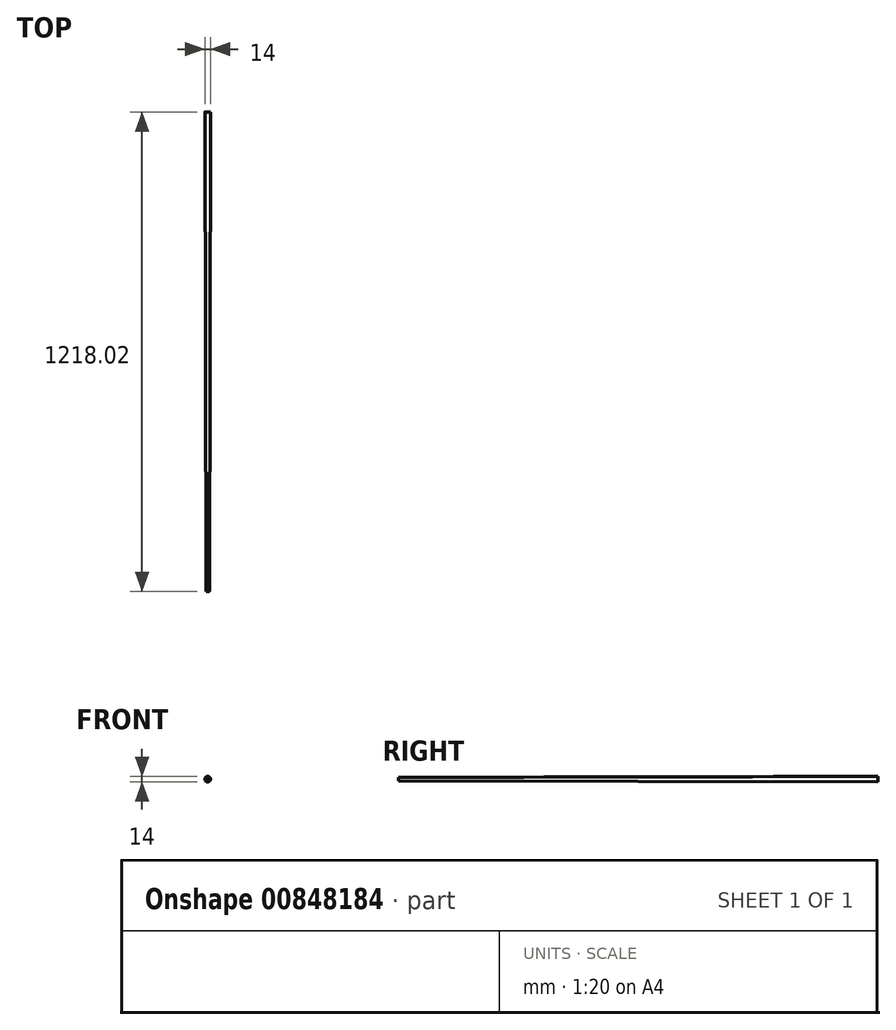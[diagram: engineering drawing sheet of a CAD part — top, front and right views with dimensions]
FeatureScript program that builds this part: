
annotation { "Feature Type Name" : "Feature", "Feature Type Description" : "" }
export const myFeature = defineFeature(function(context is Context, id is Id, definition is map)
    precondition{}
    {
        {
            var Q0;
            Q0=qCreatedBy(makeId("Right.planeOp"),FACE);
            var sketch = newSketch(context, id + "F0", { "sketchPlane" : qUnion([Q0])});
            skLineSegment(sketch, "E0", {"start": v(0, 0) * mm, "end": v(-1218.02, 0) * mm});
            skLineSegment(sketch, "E1", {"start": v(-1218.02, 0) * mm, "end": v(-1218.02, -4.42) * mm});
            skLineSegment(sketch, "E2", {"start": v(0, 0) * mm, "end": v(0, -7) * mm});
            skLineSegment(sketch, "E3", {"start": v(0, -7) * mm, "end": v(-1218.02, -4.42) * mm});
            skSolve(sketch);
        }
        {
            var Q0;
            Q0=makeQuery(id+"F0.imprint","IMPRINT",FACE,{"disambiguationData":[TD([[makeQuery(id+"F0.imprint","IMPRINT",EDGE,{"derivedFrom":sQuery(id+"F0.wireOp",EDGE,"E0")}),1.0]])]});
            var Q1;
            Q1=sQuery(id+"F0.wireOp",EDGE,"E0");
            revolve(context, id + "F1", {"surfaceOperationType" : NewSurfaceOperationType.NEW, "entities" : qUnion([Q0]), "axis" : qUnion([Q1]), "revolveType" : RevolveType.FULL});
        }
    });
